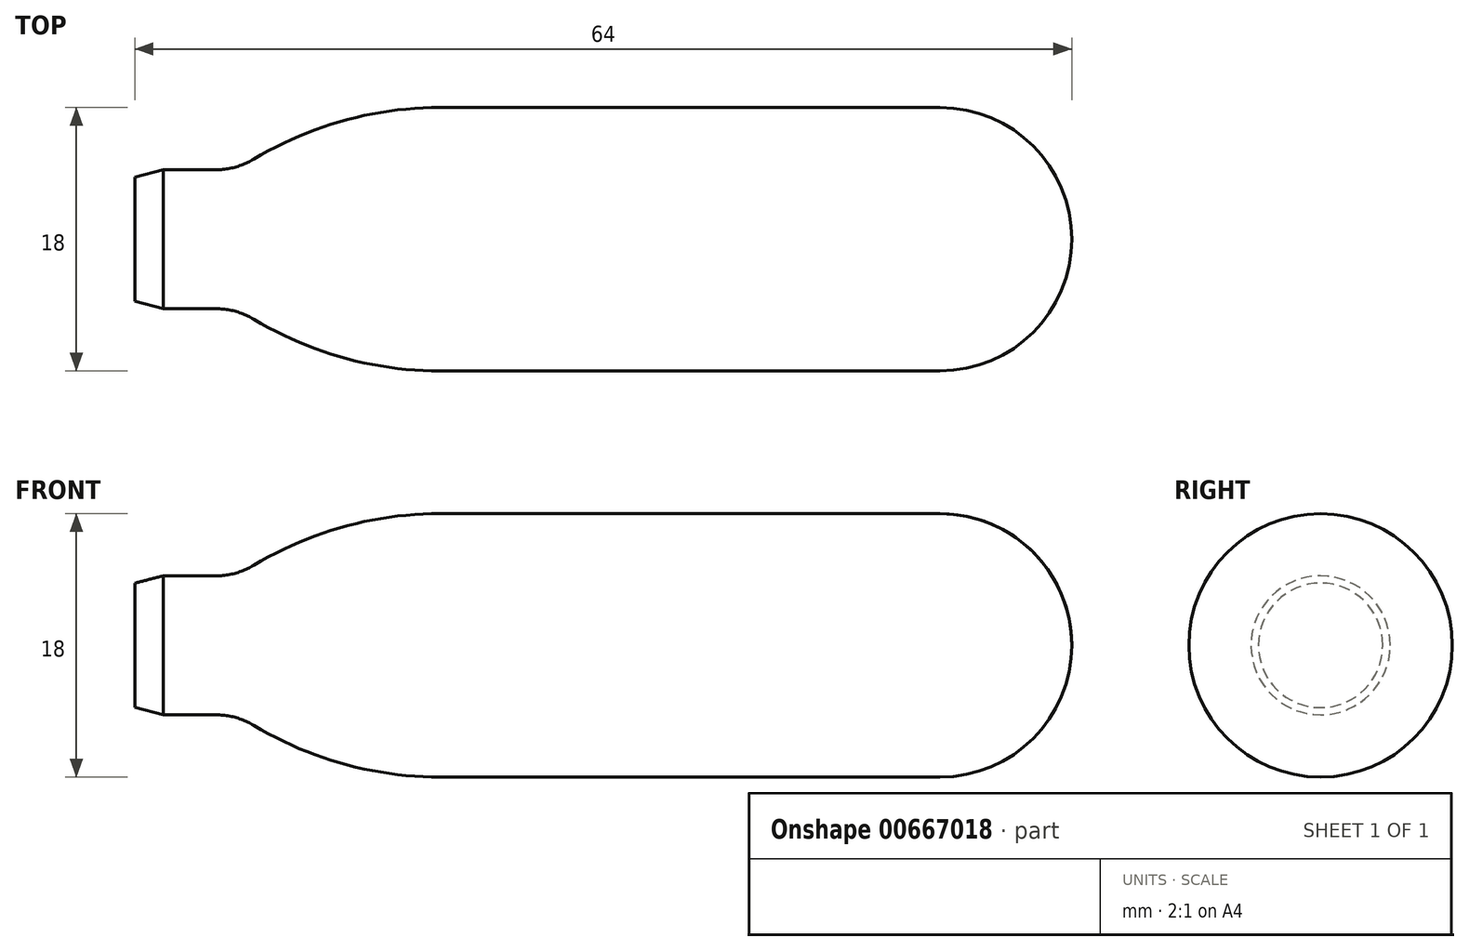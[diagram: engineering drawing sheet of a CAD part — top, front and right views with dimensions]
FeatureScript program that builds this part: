
annotation { "Feature Type Name" : "Feature", "Feature Type Description" : "" }
export const myFeature = defineFeature(function(context is Context, id is Id, definition is map)
    precondition{}
    {
        {
            var Q0;
            Q0=qCreatedBy(makeId("Front.planeOp"),FACE);
            var sketch = newSketch(context, id + "F0", { "sketchPlane" : qUnion([Q0])});
            skLineSegment(sketch, "E0", {"start": v(0, 0) * mm, "end": v(0, 4.25) * mm});
            skLineSegment(sketch, "E1", {"start": v(0, 4.25) * mm, "end": v(1.94, 4.75) * mm});
            skLineSegment(sketch, "E2", {"start": v(1.94, 4.75) * mm, "end": v(7, 4.75) * mm});
            skLineSegment(sketch, "E3", {"start": v(0, 0) * mm, "end": v(64, 0) * mm});
            skLineSegment(sketch, "E4", {"start": v(20.85, 9) * mm, "end": v(64, 9) * mm});
            skLineSegment(sketch, "E5", {"start": v(64, 0) * mm, "end": v(64, 0) * mm});
            skLineSegment(sketch, "E6", {"start": v(64, 0) * mm, "end": v(64, 9) * mm});
            skArc(sketch, "E7", {"start": v(20.85, 9) * mm, "mid": v(13.6, 7.91) * mm, "end": v(7, 4.75) * mm});
            skSolve(sketch);
        }
        {
            var Q0;
            Q0=makeQuery(id+"F0.imprint","IMPRINT",FACE,{"disambiguationData":[TD([[makeQuery(id+"F0.imprint","IMPRINT",EDGE,{"derivedFrom":sQuery(id+"F0.wireOp",EDGE,"E0")}),-1.0]])]});
            var Q1;
            Q1=sQuery(id+"F0.wireOp",EDGE,"E3");
            revolve(context, id + "F1", {"entities" : qUnion([Q0]), "axis" : qUnion([Q1]), "revolveType" : RevolveType.FULL});
        }
        {
            var Q0;
            Q0=makeQuery(id+"F1.opRevolve","SWEPT_EDGE",EDGE,{"disambiguationData":[OSD([sQuery(id+"F0.wireOp",EDGE,"E4"),sQuery(id+"F0.wireOp",EDGE,"E6")])]});
            fillet(context, id + "F2", {"entities" : qUnion([Q0]), "radius" : 9 * mm, "tangentPropagation" : true, "allowEdgeOverflow" : false});
        }
        {
            var Q0;
            Q0=makeQuery(id+"F1.opRevolve","SWEPT_EDGE",EDGE,{"disambiguationData":[OSD([sQuery(id+"F0.wireOp",EDGE,"E2"),sQuery(id+"F0.wireOp",EDGE,"E7")])]});
            fillet(context, id + "F3", {"entities" : qUnion([Q0]), "radius" : 5 * mm, "tangentPropagation" : true, "allowEdgeOverflow" : false});
        }
    });
